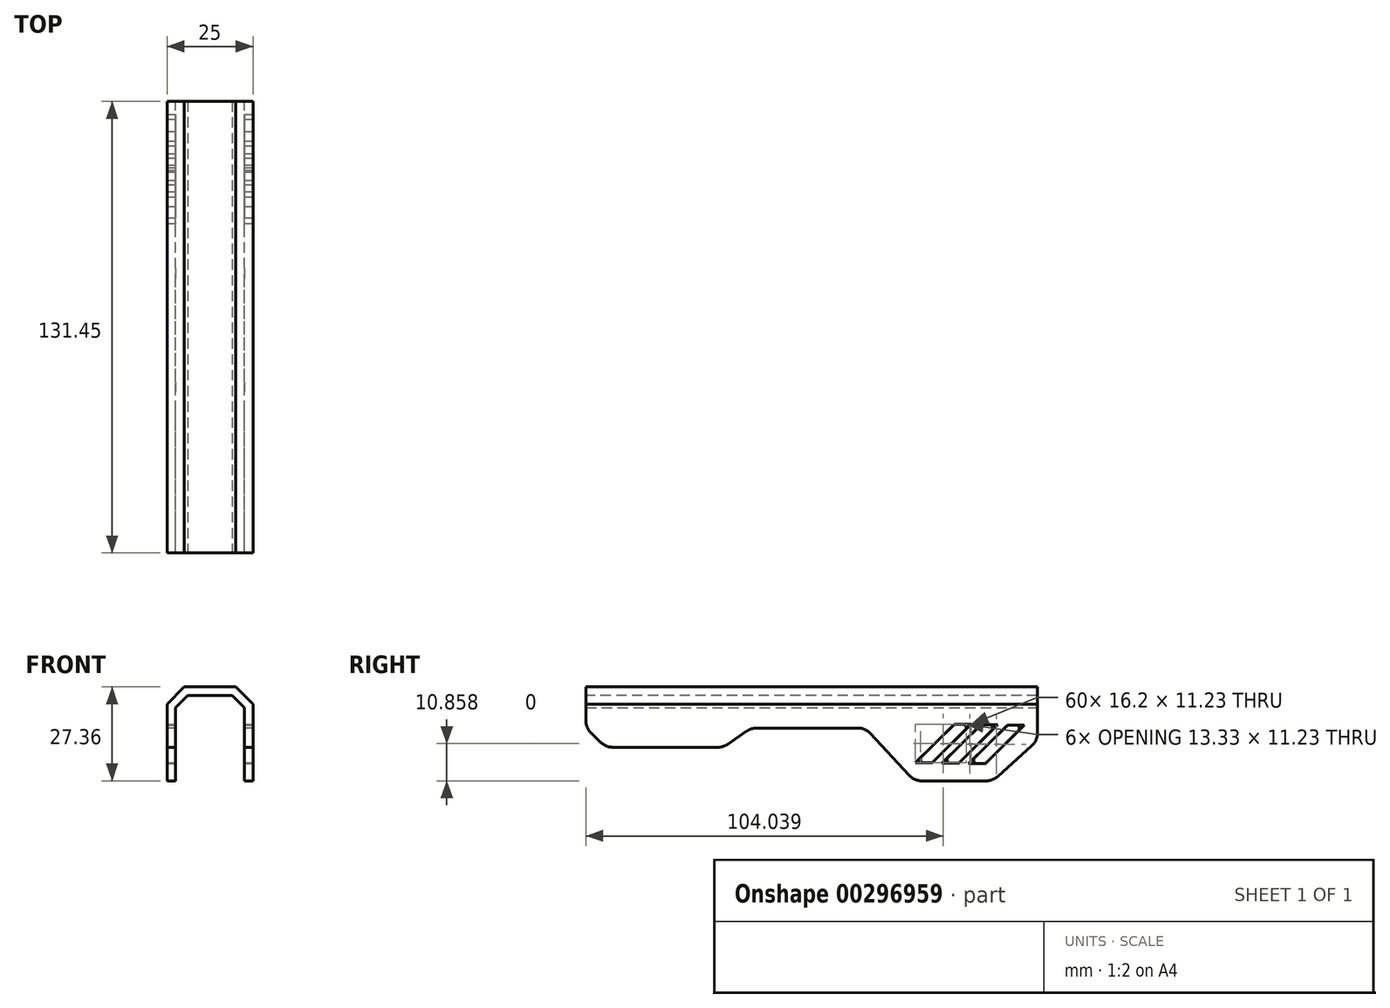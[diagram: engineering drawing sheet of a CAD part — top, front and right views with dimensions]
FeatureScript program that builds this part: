
annotation { "Feature Type Name" : "Feature", "Feature Type Description" : "" }
export const myFeature = defineFeature(function(context is Context, id is Id, definition is map)
    precondition{}
    {
        {
            var Q0;
            Q0=qCreatedBy(makeId("Right.planeOp"),FACE);
            var sketch = newSketch(context, id + "F0", { "sketchPlane" : qUnion([Q0])});
            skLineSegment(sketch, "E0.bottom", {"start": v(-66.9, 36.75) * mm, "end": v(64.56, 36.75) * mm});
            skLineSegment(sketch, "E0.top", {"start": v(-66.9, -14) * mm, "end": v(64.56, -14) * mm});
            skLineSegment(sketch, "E0.left", {"start": v(-66.9, 36.75) * mm, "end": v(-66.9, -14) * mm});
            skLineSegment(sketch, "E0.right", {"start": v(64.56, 36.75) * mm, "end": v(64.56, -14) * mm});
            skLineSegment(sketch, "E1", {"start": v(-66.9, 24.74) * mm, "end": v(-61.07, 19.17) * mm});
            skLineSegment(sketch, "E2", {"start": v(-61.07, 19.17) * mm, "end": v(-26.92, 19.17) * mm});
            skLineSegment(sketch, "E3", {"start": v(-26.92, 19.17) * mm, "end": v(-18.71, 24.77) * mm});
            skLineSegment(sketch, "E4", {"start": v(-18.71, 24.77) * mm, "end": v(14.48, 24.77) * mm});
            skLineSegment(sketch, "E5", {"start": v(14.48, 24.77) * mm, "end": v(28.75, 9.39) * mm});
            skLineSegment(sketch, "E6", {"start": v(28.75, 9.39) * mm, "end": v(51.52, 9.39) * mm});
            skLineSegment(sketch, "E7", {"start": v(51.52, 9.39) * mm, "end": v(64.56, 21.1) * mm});
            skSolve(sketch);
        }
        {
            var Q0;
            {var subQ2=sQuery(id+"F0.wireOp",EDGE,"E0.bottom");Q0=makeQuery(id+"F0.imprint","IMPRINT",FACE,{"disambiguationData":[TD([[makeQuery(id+"F0.imprint","IMPRINT",EDGE,{"derivedFrom":subQ2}),-1.0]])]});}
            extrude(context, id + "F1", {"entities" : qUnion([Q0]), "depth" : 25 * mm, "symmetric" : true});
        }
        {
            var Q0;
            Q0=makeQuery(id+"F1.opExtrude","CAP_EDGE",EDGE,{"disambiguationData":[OSD([sQuery(id+"F0.wireOp",EDGE,"E0.bottom")])],"isStart":false});
            var Q1;
            Q1=makeQuery(id+"F1.opExtrude","CAP_EDGE",EDGE,{"disambiguationData":[OSD([sQuery(id+"F0.wireOp",EDGE,"E0.bottom")])],"isStart":true});
            chamfer(context, id + "F2", {"entities" : qUnion([Q0, Q1]), "width" : 5 * mm, "tangentPropagation" : true});
        }
        {
            var Q0;
            Q0=makeQuery(id+"F1.opExtrude","SWEPT_FACE",FACE,{"disambiguationData":[OSD([sQuery(id+"F0.wireOp",EDGE,"E0.left")])]});
            var Q1;
            Q1=makeQuery(id+"F1.opExtrude","SWEPT_FACE",FACE,{"disambiguationData":[OSD([sQuery(id+"F0.wireOp",EDGE,"E1")])]});
            var Q2;
            Q2=makeQuery(id+"F1.opExtrude","SWEPT_FACE",FACE,{"disambiguationData":[OSD([sQuery(id+"F0.wireOp",EDGE,"E2")])]});
            var Q3;
            Q3=makeQuery(id+"F1.opExtrude","SWEPT_FACE",FACE,{"disambiguationData":[OSD([sQuery(id+"F0.wireOp",EDGE,"E3")])]});
            var Q4;
            Q4=makeQuery(id+"F1.opExtrude","SWEPT_FACE",FACE,{"disambiguationData":[OSD([sQuery(id+"F0.wireOp",EDGE,"E4")])]});
            var Q5;
            Q5=makeQuery(id+"F1.opExtrude","SWEPT_FACE",FACE,{"disambiguationData":[OSD([sQuery(id+"F0.wireOp",EDGE,"E5")])]});
            var Q6;
            Q6=makeQuery(id+"F1.opExtrude","SWEPT_FACE",FACE,{"disambiguationData":[OSD([sQuery(id+"F0.wireOp",EDGE,"E6")])]});
            var Q7;
            Q7=makeQuery(id+"F1.opExtrude","SWEPT_FACE",FACE,{"disambiguationData":[OSD([sQuery(id+"F0.wireOp",EDGE,"E7")])]});
            var Q8;
            Q8=makeQuery(id+"F1.opExtrude","SWEPT_FACE",FACE,{"disambiguationData":[OSD([sQuery(id+"F0.wireOp",EDGE,"E0.right")])]});
            shell(context, id + "F3", {"entities" : qUnion([Q0, Q1, Q2, Q3, Q4, Q5, Q6, Q7, Q8]), "thickness" : 2.5 * mm});
        }
        {
            var Q0;
            Q0=makeQuery(id+"F1.opExtrude","SWEPT_EDGE",EDGE,{"disambiguationData":[OSD([sQuery(id+"F0.wireOp",EDGE,"E0.left"),sQuery(id+"F0.wireOp",EDGE,"E1")])]});
            var Q1;
            Q1=makeQuery(id+"F1.opExtrude","SWEPT_EDGE",EDGE,{"disambiguationData":[OSD([sQuery(id+"F0.wireOp",EDGE,"E1"),sQuery(id+"F0.wireOp",EDGE,"E2")])]});
            var Q2;
            Q2=makeQuery(id+"F1.opExtrude","SWEPT_EDGE",EDGE,{"disambiguationData":[OSD([sQuery(id+"F0.wireOp",EDGE,"E2"),sQuery(id+"F0.wireOp",EDGE,"E3")])]});
            var Q3;
            Q3=makeQuery(id+"F1.opExtrude","SWEPT_EDGE",EDGE,{"disambiguationData":[OSD([sQuery(id+"F0.wireOp",EDGE,"E3"),sQuery(id+"F0.wireOp",EDGE,"E4")])]});
            var Q4;
            Q4=makeQuery(id+"F1.opExtrude","SWEPT_EDGE",EDGE,{"disambiguationData":[OSD([sQuery(id+"F0.wireOp",EDGE,"E4"),sQuery(id+"F0.wireOp",EDGE,"E5")])]});
            var Q5;
            Q5=makeQuery(id+"F1.opExtrude","SWEPT_EDGE",EDGE,{"disambiguationData":[OSD([sQuery(id+"F0.wireOp",EDGE,"E5"),sQuery(id+"F0.wireOp",EDGE,"E6")])]});
            var Q6;
            Q6=makeQuery(id+"F1.opExtrude","SWEPT_EDGE",EDGE,{"disambiguationData":[OSD([sQuery(id+"F0.wireOp",EDGE,"E6"),sQuery(id+"F0.wireOp",EDGE,"E7")])]});
            var Q7;
            Q7=makeQuery(id+"F1.opExtrude","SWEPT_EDGE",EDGE,{"disambiguationData":[OSD([sQuery(id+"F0.wireOp",EDGE,"E0.right"),sQuery(id+"F0.wireOp",EDGE,"E7")])]});
            var Q8;
            Q8=makeQuery(id+"F3.opShell","OFFSET_EDGE",EDGE,{"disambiguationData":[OSD([sQuery(id+"F0.wireOp",EDGE,"E0.left"),sQuery(id+"F0.wireOp",EDGE,"E1")])]});
            var Q9;
            Q9=makeQuery(id+"F3.opShell","OFFSET_EDGE",EDGE,{"disambiguationData":[OSD([sQuery(id+"F0.wireOp",EDGE,"E1"),sQuery(id+"F0.wireOp",EDGE,"E2")])]});
            var Q10;
            Q10=makeQuery(id+"F3.opShell","OFFSET_EDGE",EDGE,{"disambiguationData":[OSD([sQuery(id+"F0.wireOp",EDGE,"E2"),sQuery(id+"F0.wireOp",EDGE,"E3")])]});
            var Q11;
            Q11=makeQuery(id+"F3.opShell","OFFSET_EDGE",EDGE,{"disambiguationData":[OSD([sQuery(id+"F0.wireOp",EDGE,"E3"),sQuery(id+"F0.wireOp",EDGE,"E4")])]});
            var Q12;
            Q12=makeQuery(id+"F3.opShell","OFFSET_EDGE",EDGE,{"disambiguationData":[OSD([sQuery(id+"F0.wireOp",EDGE,"E4"),sQuery(id+"F0.wireOp",EDGE,"E5")])]});
            var Q13;
            Q13=makeQuery(id+"F3.opShell","OFFSET_EDGE",EDGE,{"disambiguationData":[OSD([sQuery(id+"F0.wireOp",EDGE,"E5"),sQuery(id+"F0.wireOp",EDGE,"E6")])]});
            var Q14;
            Q14=makeQuery(id+"F3.opShell","OFFSET_EDGE",EDGE,{"disambiguationData":[OSD([sQuery(id+"F0.wireOp",EDGE,"E6"),sQuery(id+"F0.wireOp",EDGE,"E7")])]});
            var Q15;
            Q15=makeQuery(id+"F3.opShell","OFFSET_EDGE",EDGE,{"disambiguationData":[OSD([sQuery(id+"F0.wireOp",EDGE,"E0.right"),sQuery(id+"F0.wireOp",EDGE,"E7")])]});
            fillet(context, id + "F4", {"entities" : qUnion([Q0, Q1, Q2, Q3, Q4, Q5, Q6, Q7, Q8, Q9, Q10, Q11, Q12, Q13, Q14, Q15]), "radius" : 5 * mm, "tangentPropagation" : true, "allowEdgeOverflow" : false});
        }
        {
            var Q0;
            Q0=qCreatedBy(makeId("Right.planeOp"),FACE);
            var sketch = newSketch(context, id + "F5", { "sketchPlane" : qUnion([Q0])});
            skLineSegment(sketch, "E8", {"start": v(60.73, 25.66) * mm, "end": v(49.4, 14.44) * mm});
            skLineSegment(sketch, "E9", {"start": v(49.4, 14.44) * mm, "end": v(44.53, 14.44) * mm});
            skLineSegment(sketch, "E10", {"start": v(44.53, 14.44) * mm, "end": v(55.87, 25.66) * mm});
            skLineSegment(sketch, "E11", {"start": v(55.87, 25.66) * mm, "end": v(60.73, 25.66) * mm});
            skLineSegment(sketch, "E12.1.0.0", {"start": v(36.8, 14.54) * mm, "end": v(48.13, 25.76) * mm});
            skLineSegment(sketch, "E12.1.0.1", {"start": v(52.99, 25.76) * mm, "end": v(41.65, 14.54) * mm});
            skLineSegment(sketch, "E12.1.0.2", {"start": v(48.13, 25.76) * mm, "end": v(52.99, 25.76) * mm});
            skLineSegment(sketch, "E12.1.0.3", {"start": v(41.65, 14.54) * mm, "end": v(36.8, 14.54) * mm});
            skLineSegment(sketch, "E12.2.0.0", {"start": v(29.05, 14.63) * mm, "end": v(40.39, 25.86) * mm});
            skLineSegment(sketch, "E12.2.0.1", {"start": v(45.25, 25.86) * mm, "end": v(33.91, 14.63) * mm});
            skLineSegment(sketch, "E12.2.0.2", {"start": v(40.39, 25.86) * mm, "end": v(45.25, 25.86) * mm});
            skLineSegment(sketch, "E12.2.0.3", {"start": v(33.91, 14.63) * mm, "end": v(29.05, 14.63) * mm});
            skLineSegment(sketch, "E12.direction1", {"start": v(44.53, 14.44) * mm, "end": v(36.8, 14.54) * mm, "construction": true});
            skSolve(sketch);
        }
        {
            var Q0;
            Q0 = qSketchRegion(id + "F5", true);
            extrude(context, id + "F6", {"entities" : qUnion([Q0]), "operationType" : NewBodyOperationType.REMOVE, "oppositeDirection" : true, "depth" : 25 * mm, "symmetric" : true});
        }
        {
            var Q0;
            {var subQ0=sQuery(id+"F0.wireOp",EDGE,"E7");var subQ1=sQuery(id+"F0.wireOp",EDGE,"E6");var subQ2=sQuery(id+"F0.wireOp",EDGE,"E5");var subQ3=sQuery(id+"F0.wireOp",EDGE,"E4");var subQ4=sQuery(id+"F0.wireOp",EDGE,"E3");var subQ5=sQuery(id+"F0.wireOp",EDGE,"E2");var subQ6=sQuery(id+"F0.wireOp",EDGE,"E1");var subQ7=sQuery(id+"F0.wireOp",EDGE,"E0.right");var subQ8=sQuery(id+"F0.wireOp",EDGE,"E0.left");var subQ9=sQuery(id+"F0.wireOp",EDGE,"E0.bottom");var subQ10=makeQuery(id+"F1.opExtrude","CAP_FACE",FACE,{"disambiguationData":[OSD([subQ9,subQ8,subQ7,subQ6,subQ5,subQ4,subQ3,subQ2,subQ1,subQ0])],"isStart":true});var subQ11=sQuery(id+"F5.wireOp",EDGE,"E8");var subQ12=sQuery(id+"F5.wireOp",EDGE,"E11");Q0=makeQuery(id+"F6.boolean.opBoolean","COPY",EDGE,{"disambiguationData":[TD([subQ10])],"derivedFrom":makeQuery(id+"F6.opExtrude","SWEPT_EDGE",EDGE,{"disambiguationData":[OSD([subQ11,subQ12])]})});}
            var Q1;
            {var subQ0=sQuery(id+"F0.wireOp",EDGE,"E7");var subQ1=sQuery(id+"F0.wireOp",EDGE,"E6");var subQ2=sQuery(id+"F0.wireOp",EDGE,"E5");var subQ3=sQuery(id+"F0.wireOp",EDGE,"E4");var subQ4=sQuery(id+"F0.wireOp",EDGE,"E3");var subQ5=sQuery(id+"F0.wireOp",EDGE,"E2");var subQ6=sQuery(id+"F0.wireOp",EDGE,"E1");var subQ7=sQuery(id+"F0.wireOp",EDGE,"E0.right");var subQ8=sQuery(id+"F0.wireOp",EDGE,"E0.left");var subQ9=sQuery(id+"F0.wireOp",EDGE,"E0.bottom");var subQ10=makeQuery(id+"F1.opExtrude","CAP_FACE",FACE,{"disambiguationData":[OSD([subQ9,subQ8,subQ7,subQ6,subQ5,subQ4,subQ3,subQ2,subQ1,subQ0])],"isStart":true});var subQ11=sQuery(id+"F5.wireOp",EDGE,"E11");var subQ12=sQuery(id+"F5.wireOp",EDGE,"E10");Q1=makeQuery(id+"F6.boolean.opBoolean","COPY",EDGE,{"disambiguationData":[TD([subQ10])],"derivedFrom":makeQuery(id+"F6.opExtrude","SWEPT_EDGE",EDGE,{"disambiguationData":[OSD([subQ12,subQ11])]})});}
            var Q2;
            {var subQ0=sQuery(id+"F0.wireOp",EDGE,"E7");var subQ1=sQuery(id+"F0.wireOp",EDGE,"E6");var subQ2=sQuery(id+"F0.wireOp",EDGE,"E5");var subQ3=sQuery(id+"F0.wireOp",EDGE,"E4");var subQ4=sQuery(id+"F0.wireOp",EDGE,"E3");var subQ5=sQuery(id+"F0.wireOp",EDGE,"E2");var subQ6=sQuery(id+"F0.wireOp",EDGE,"E1");var subQ7=sQuery(id+"F0.wireOp",EDGE,"E0.right");var subQ8=sQuery(id+"F0.wireOp",EDGE,"E0.left");var subQ9=sQuery(id+"F0.wireOp",EDGE,"E0.bottom");var subQ10=makeQuery(id+"F1.opExtrude","CAP_FACE",FACE,{"disambiguationData":[OSD([subQ9,subQ8,subQ7,subQ6,subQ5,subQ4,subQ3,subQ2,subQ1,subQ0])],"isStart":true});var subQ11=sQuery(id+"F5.wireOp",EDGE,"E9");var subQ12=sQuery(id+"F5.wireOp",EDGE,"E10");Q2=makeQuery(id+"F6.boolean.opBoolean","COPY",EDGE,{"disambiguationData":[TD([subQ10])],"derivedFrom":makeQuery(id+"F6.opExtrude","SWEPT_EDGE",EDGE,{"disambiguationData":[OSD([subQ11,subQ12])]})});}
            var Q3;
            {var subQ0=sQuery(id+"F0.wireOp",EDGE,"E7");var subQ1=sQuery(id+"F0.wireOp",EDGE,"E6");var subQ2=sQuery(id+"F0.wireOp",EDGE,"E5");var subQ3=sQuery(id+"F0.wireOp",EDGE,"E4");var subQ4=sQuery(id+"F0.wireOp",EDGE,"E3");var subQ5=sQuery(id+"F0.wireOp",EDGE,"E2");var subQ6=sQuery(id+"F0.wireOp",EDGE,"E1");var subQ7=sQuery(id+"F0.wireOp",EDGE,"E0.right");var subQ8=sQuery(id+"F0.wireOp",EDGE,"E0.left");var subQ9=sQuery(id+"F0.wireOp",EDGE,"E0.bottom");var subQ10=makeQuery(id+"F1.opExtrude","CAP_FACE",FACE,{"disambiguationData":[OSD([subQ9,subQ8,subQ7,subQ6,subQ5,subQ4,subQ3,subQ2,subQ1,subQ0])],"isStart":true});var subQ11=sQuery(id+"F5.wireOp",EDGE,"E12.1.0.0");var subQ12=sQuery(id+"F5.wireOp",EDGE,"E12.1.0.3");Q3=makeQuery(id+"F6.boolean.opBoolean","COPY",EDGE,{"disambiguationData":[TD([subQ10])],"derivedFrom":makeQuery(id+"F6.opExtrude","SWEPT_EDGE",EDGE,{"disambiguationData":[OSD([subQ11,subQ12])]})});}
            var Q4;
            {var subQ0=sQuery(id+"F0.wireOp",EDGE,"E7");var subQ1=sQuery(id+"F0.wireOp",EDGE,"E6");var subQ2=sQuery(id+"F0.wireOp",EDGE,"E5");var subQ3=sQuery(id+"F0.wireOp",EDGE,"E4");var subQ4=sQuery(id+"F0.wireOp",EDGE,"E3");var subQ5=sQuery(id+"F0.wireOp",EDGE,"E2");var subQ6=sQuery(id+"F0.wireOp",EDGE,"E1");var subQ7=sQuery(id+"F0.wireOp",EDGE,"E0.right");var subQ8=sQuery(id+"F0.wireOp",EDGE,"E0.left");var subQ9=sQuery(id+"F0.wireOp",EDGE,"E0.bottom");var subQ10=makeQuery(id+"F1.opExtrude","CAP_FACE",FACE,{"disambiguationData":[OSD([subQ9,subQ8,subQ7,subQ6,subQ5,subQ4,subQ3,subQ2,subQ1,subQ0])],"isStart":true});var subQ11=sQuery(id+"F5.wireOp",EDGE,"E12.2.0.0");var subQ12=sQuery(id+"F5.wireOp",EDGE,"E12.2.0.3");Q4=makeQuery(id+"F6.boolean.opBoolean","COPY",EDGE,{"disambiguationData":[TD([subQ10])],"derivedFrom":makeQuery(id+"F6.opExtrude","SWEPT_EDGE",EDGE,{"disambiguationData":[OSD([subQ11,subQ12])]})});}
            var Q5;
            {var subQ0=sQuery(id+"F0.wireOp",EDGE,"E7");var subQ1=sQuery(id+"F0.wireOp",EDGE,"E6");var subQ2=sQuery(id+"F0.wireOp",EDGE,"E5");var subQ3=sQuery(id+"F0.wireOp",EDGE,"E4");var subQ4=sQuery(id+"F0.wireOp",EDGE,"E3");var subQ5=sQuery(id+"F0.wireOp",EDGE,"E2");var subQ6=sQuery(id+"F0.wireOp",EDGE,"E1");var subQ7=sQuery(id+"F0.wireOp",EDGE,"E0.right");var subQ8=sQuery(id+"F0.wireOp",EDGE,"E0.left");var subQ9=sQuery(id+"F0.wireOp",EDGE,"E0.bottom");var subQ10=makeQuery(id+"F1.opExtrude","CAP_FACE",FACE,{"disambiguationData":[OSD([subQ9,subQ8,subQ7,subQ6,subQ5,subQ4,subQ3,subQ2,subQ1,subQ0])],"isStart":true});var subQ11=sQuery(id+"F5.wireOp",EDGE,"E8");var subQ12=sQuery(id+"F5.wireOp",EDGE,"E9");Q5=makeQuery(id+"F6.boolean.opBoolean","COPY",EDGE,{"disambiguationData":[TD([subQ10])],"derivedFrom":makeQuery(id+"F6.opExtrude","SWEPT_EDGE",EDGE,{"disambiguationData":[OSD([subQ11,subQ12])]})});}
            var Q6;
            {var subQ0=sQuery(id+"F0.wireOp",EDGE,"E7");var subQ1=sQuery(id+"F0.wireOp",EDGE,"E6");var subQ2=sQuery(id+"F0.wireOp",EDGE,"E5");var subQ3=sQuery(id+"F0.wireOp",EDGE,"E4");var subQ4=sQuery(id+"F0.wireOp",EDGE,"E3");var subQ5=sQuery(id+"F0.wireOp",EDGE,"E2");var subQ6=sQuery(id+"F0.wireOp",EDGE,"E1");var subQ7=sQuery(id+"F0.wireOp",EDGE,"E0.right");var subQ8=sQuery(id+"F0.wireOp",EDGE,"E0.left");var subQ9=sQuery(id+"F0.wireOp",EDGE,"E0.bottom");var subQ10=makeQuery(id+"F1.opExtrude","CAP_FACE",FACE,{"disambiguationData":[OSD([subQ9,subQ8,subQ7,subQ6,subQ5,subQ4,subQ3,subQ2,subQ1,subQ0])],"isStart":true});var subQ11=sQuery(id+"F5.wireOp",EDGE,"E12.1.0.3");var subQ12=sQuery(id+"F5.wireOp",EDGE,"E12.1.0.1");Q6=makeQuery(id+"F6.boolean.opBoolean","COPY",EDGE,{"disambiguationData":[TD([subQ10])],"derivedFrom":makeQuery(id+"F6.opExtrude","SWEPT_EDGE",EDGE,{"disambiguationData":[OSD([subQ12,subQ11])]})});}
            var Q7;
            {var subQ0=sQuery(id+"F0.wireOp",EDGE,"E7");var subQ1=sQuery(id+"F0.wireOp",EDGE,"E6");var subQ2=sQuery(id+"F0.wireOp",EDGE,"E5");var subQ3=sQuery(id+"F0.wireOp",EDGE,"E4");var subQ4=sQuery(id+"F0.wireOp",EDGE,"E3");var subQ5=sQuery(id+"F0.wireOp",EDGE,"E2");var subQ6=sQuery(id+"F0.wireOp",EDGE,"E1");var subQ7=sQuery(id+"F0.wireOp",EDGE,"E0.right");var subQ8=sQuery(id+"F0.wireOp",EDGE,"E0.left");var subQ9=sQuery(id+"F0.wireOp",EDGE,"E0.bottom");var subQ10=makeQuery(id+"F1.opExtrude","CAP_FACE",FACE,{"disambiguationData":[OSD([subQ9,subQ8,subQ7,subQ6,subQ5,subQ4,subQ3,subQ2,subQ1,subQ0])],"isStart":true});var subQ11=sQuery(id+"F5.wireOp",EDGE,"E12.2.0.1");var subQ12=sQuery(id+"F5.wireOp",EDGE,"E12.2.0.3");Q7=makeQuery(id+"F6.boolean.opBoolean","COPY",EDGE,{"disambiguationData":[TD([subQ10])],"derivedFrom":makeQuery(id+"F6.opExtrude","SWEPT_EDGE",EDGE,{"disambiguationData":[OSD([subQ11,subQ12])]})});}
            var Q8;
            {var subQ0=sQuery(id+"F0.wireOp",EDGE,"E7");var subQ1=sQuery(id+"F0.wireOp",EDGE,"E6");var subQ2=sQuery(id+"F0.wireOp",EDGE,"E5");var subQ3=sQuery(id+"F0.wireOp",EDGE,"E4");var subQ4=sQuery(id+"F0.wireOp",EDGE,"E3");var subQ5=sQuery(id+"F0.wireOp",EDGE,"E2");var subQ6=sQuery(id+"F0.wireOp",EDGE,"E1");var subQ7=sQuery(id+"F0.wireOp",EDGE,"E0.right");var subQ8=sQuery(id+"F0.wireOp",EDGE,"E0.left");var subQ9=sQuery(id+"F0.wireOp",EDGE,"E0.bottom");var subQ10=makeQuery(id+"F1.opExtrude","CAP_FACE",FACE,{"disambiguationData":[OSD([subQ9,subQ8,subQ7,subQ6,subQ5,subQ4,subQ3,subQ2,subQ1,subQ0])],"isStart":true});var subQ11=sQuery(id+"F5.wireOp",EDGE,"E12.1.0.2");var subQ12=sQuery(id+"F5.wireOp",EDGE,"E12.1.0.1");Q8=makeQuery(id+"F6.boolean.opBoolean","COPY",EDGE,{"disambiguationData":[TD([subQ10])],"derivedFrom":makeQuery(id+"F6.opExtrude","SWEPT_EDGE",EDGE,{"disambiguationData":[OSD([subQ12,subQ11])]})});}
            var Q9;
            {var subQ0=sQuery(id+"F0.wireOp",EDGE,"E7");var subQ1=sQuery(id+"F0.wireOp",EDGE,"E6");var subQ2=sQuery(id+"F0.wireOp",EDGE,"E5");var subQ3=sQuery(id+"F0.wireOp",EDGE,"E4");var subQ4=sQuery(id+"F0.wireOp",EDGE,"E3");var subQ5=sQuery(id+"F0.wireOp",EDGE,"E2");var subQ6=sQuery(id+"F0.wireOp",EDGE,"E1");var subQ7=sQuery(id+"F0.wireOp",EDGE,"E0.right");var subQ8=sQuery(id+"F0.wireOp",EDGE,"E0.left");var subQ9=sQuery(id+"F0.wireOp",EDGE,"E0.bottom");var subQ10=makeQuery(id+"F1.opExtrude","CAP_FACE",FACE,{"disambiguationData":[OSD([subQ9,subQ8,subQ7,subQ6,subQ5,subQ4,subQ3,subQ2,subQ1,subQ0])],"isStart":true});var subQ11=sQuery(id+"F5.wireOp",EDGE,"E12.2.0.1");var subQ12=sQuery(id+"F5.wireOp",EDGE,"E12.2.0.2");Q9=makeQuery(id+"F6.boolean.opBoolean","COPY",EDGE,{"disambiguationData":[TD([subQ10])],"derivedFrom":makeQuery(id+"F6.opExtrude","SWEPT_EDGE",EDGE,{"disambiguationData":[OSD([subQ11,subQ12])]})});}
            var Q10;
            {var subQ0=sQuery(id+"F0.wireOp",EDGE,"E7");var subQ1=sQuery(id+"F0.wireOp",EDGE,"E6");var subQ2=sQuery(id+"F0.wireOp",EDGE,"E5");var subQ3=sQuery(id+"F0.wireOp",EDGE,"E4");var subQ4=sQuery(id+"F0.wireOp",EDGE,"E3");var subQ5=sQuery(id+"F0.wireOp",EDGE,"E2");var subQ6=sQuery(id+"F0.wireOp",EDGE,"E1");var subQ7=sQuery(id+"F0.wireOp",EDGE,"E0.right");var subQ8=sQuery(id+"F0.wireOp",EDGE,"E0.left");var subQ9=sQuery(id+"F0.wireOp",EDGE,"E0.bottom");var subQ10=makeQuery(id+"F1.opExtrude","CAP_FACE",FACE,{"disambiguationData":[OSD([subQ9,subQ8,subQ7,subQ6,subQ5,subQ4,subQ3,subQ2,subQ1,subQ0])],"isStart":true});var subQ11=sQuery(id+"F5.wireOp",EDGE,"E12.2.0.2");var subQ12=sQuery(id+"F5.wireOp",EDGE,"E12.2.0.0");Q10=makeQuery(id+"F6.boolean.opBoolean","COPY",EDGE,{"disambiguationData":[TD([subQ10])],"derivedFrom":makeQuery(id+"F6.opExtrude","SWEPT_EDGE",EDGE,{"disambiguationData":[OSD([subQ12,subQ11])]})});}
            var Q11;
            {var subQ0=sQuery(id+"F0.wireOp",EDGE,"E7");var subQ1=sQuery(id+"F0.wireOp",EDGE,"E6");var subQ2=sQuery(id+"F0.wireOp",EDGE,"E5");var subQ3=sQuery(id+"F0.wireOp",EDGE,"E4");var subQ4=sQuery(id+"F0.wireOp",EDGE,"E3");var subQ5=sQuery(id+"F0.wireOp",EDGE,"E2");var subQ6=sQuery(id+"F0.wireOp",EDGE,"E1");var subQ7=sQuery(id+"F0.wireOp",EDGE,"E0.right");var subQ8=sQuery(id+"F0.wireOp",EDGE,"E0.left");var subQ9=sQuery(id+"F0.wireOp",EDGE,"E0.bottom");var subQ10=makeQuery(id+"F1.opExtrude","CAP_FACE",FACE,{"disambiguationData":[OSD([subQ9,subQ8,subQ7,subQ6,subQ5,subQ4,subQ3,subQ2,subQ1,subQ0])],"isStart":true});var subQ11=sQuery(id+"F5.wireOp",EDGE,"E12.1.0.2");var subQ12=sQuery(id+"F5.wireOp",EDGE,"E12.1.0.0");Q11=makeQuery(id+"F6.boolean.opBoolean","COPY",EDGE,{"disambiguationData":[TD([subQ10])],"derivedFrom":makeQuery(id+"F6.opExtrude","SWEPT_EDGE",EDGE,{"disambiguationData":[OSD([subQ12,subQ11])]})});}
            var Q12;
            {var subQ0=sQuery(id+"F0.wireOp",EDGE,"E7");var subQ1=sQuery(id+"F0.wireOp",EDGE,"E6");var subQ2=sQuery(id+"F0.wireOp",EDGE,"E5");var subQ3=sQuery(id+"F0.wireOp",EDGE,"E4");var subQ4=sQuery(id+"F0.wireOp",EDGE,"E3");var subQ5=sQuery(id+"F0.wireOp",EDGE,"E2");var subQ6=sQuery(id+"F0.wireOp",EDGE,"E1");var subQ7=sQuery(id+"F0.wireOp",EDGE,"E0.right");var subQ8=sQuery(id+"F0.wireOp",EDGE,"E0.left");var subQ9=sQuery(id+"F0.wireOp",EDGE,"E0.bottom");var subQ10=makeQuery(id+"F1.opExtrude","CAP_FACE",FACE,{"disambiguationData":[OSD([subQ9,subQ8,subQ7,subQ6,subQ5,subQ4,subQ3,subQ2,subQ1,subQ0])],"isStart":false});var subQ11=sQuery(id+"F5.wireOp",EDGE,"E8");var subQ12=sQuery(id+"F5.wireOp",EDGE,"E11");Q12=makeQuery(id+"F6.boolean.opBoolean","COPY",EDGE,{"disambiguationData":[TD([subQ10])],"derivedFrom":makeQuery(id+"F6.opExtrude","SWEPT_EDGE",EDGE,{"disambiguationData":[OSD([subQ11,subQ12])]})});}
            var Q13;
            {var subQ0=sQuery(id+"F0.wireOp",EDGE,"E7");var subQ1=sQuery(id+"F0.wireOp",EDGE,"E6");var subQ2=sQuery(id+"F0.wireOp",EDGE,"E5");var subQ3=sQuery(id+"F0.wireOp",EDGE,"E4");var subQ4=sQuery(id+"F0.wireOp",EDGE,"E3");var subQ5=sQuery(id+"F0.wireOp",EDGE,"E2");var subQ6=sQuery(id+"F0.wireOp",EDGE,"E1");var subQ7=sQuery(id+"F0.wireOp",EDGE,"E0.right");var subQ8=sQuery(id+"F0.wireOp",EDGE,"E0.left");var subQ9=sQuery(id+"F0.wireOp",EDGE,"E0.bottom");var subQ10=makeQuery(id+"F1.opExtrude","CAP_FACE",FACE,{"disambiguationData":[OSD([subQ9,subQ8,subQ7,subQ6,subQ5,subQ4,subQ3,subQ2,subQ1,subQ0])],"isStart":false});var subQ11=sQuery(id+"F5.wireOp",EDGE,"E12.1.0.1");var subQ12=sQuery(id+"F5.wireOp",EDGE,"E12.1.0.2");Q13=makeQuery(id+"F6.boolean.opBoolean","COPY",EDGE,{"disambiguationData":[TD([subQ10])],"derivedFrom":makeQuery(id+"F6.opExtrude","SWEPT_EDGE",EDGE,{"disambiguationData":[OSD([subQ11,subQ12])]})});}
            var Q14;
            {var subQ0=sQuery(id+"F0.wireOp",EDGE,"E7");var subQ1=sQuery(id+"F0.wireOp",EDGE,"E6");var subQ2=sQuery(id+"F0.wireOp",EDGE,"E5");var subQ3=sQuery(id+"F0.wireOp",EDGE,"E4");var subQ4=sQuery(id+"F0.wireOp",EDGE,"E3");var subQ5=sQuery(id+"F0.wireOp",EDGE,"E2");var subQ6=sQuery(id+"F0.wireOp",EDGE,"E1");var subQ7=sQuery(id+"F0.wireOp",EDGE,"E0.right");var subQ8=sQuery(id+"F0.wireOp",EDGE,"E0.left");var subQ9=sQuery(id+"F0.wireOp",EDGE,"E0.bottom");var subQ10=makeQuery(id+"F1.opExtrude","CAP_FACE",FACE,{"disambiguationData":[OSD([subQ9,subQ8,subQ7,subQ6,subQ5,subQ4,subQ3,subQ2,subQ1,subQ0])],"isStart":false});var subQ11=sQuery(id+"F5.wireOp",EDGE,"E12.2.0.2");var subQ12=sQuery(id+"F5.wireOp",EDGE,"E12.2.0.1");Q14=makeQuery(id+"F6.boolean.opBoolean","COPY",EDGE,{"disambiguationData":[TD([subQ10])],"derivedFrom":makeQuery(id+"F6.opExtrude","SWEPT_EDGE",EDGE,{"disambiguationData":[OSD([subQ12,subQ11])]})});}
            var Q15;
            {var subQ0=sQuery(id+"F0.wireOp",EDGE,"E7");var subQ1=sQuery(id+"F0.wireOp",EDGE,"E6");var subQ2=sQuery(id+"F0.wireOp",EDGE,"E5");var subQ3=sQuery(id+"F0.wireOp",EDGE,"E4");var subQ4=sQuery(id+"F0.wireOp",EDGE,"E3");var subQ5=sQuery(id+"F0.wireOp",EDGE,"E2");var subQ6=sQuery(id+"F0.wireOp",EDGE,"E1");var subQ7=sQuery(id+"F0.wireOp",EDGE,"E0.right");var subQ8=sQuery(id+"F0.wireOp",EDGE,"E0.left");var subQ9=sQuery(id+"F0.wireOp",EDGE,"E0.bottom");var subQ10=makeQuery(id+"F1.opExtrude","CAP_FACE",FACE,{"disambiguationData":[OSD([subQ9,subQ8,subQ7,subQ6,subQ5,subQ4,subQ3,subQ2,subQ1,subQ0])],"isStart":false});var subQ11=sQuery(id+"F5.wireOp",EDGE,"E8");var subQ12=sQuery(id+"F5.wireOp",EDGE,"E9");Q15=makeQuery(id+"F6.boolean.opBoolean","COPY",EDGE,{"disambiguationData":[TD([subQ10])],"derivedFrom":makeQuery(id+"F6.opExtrude","SWEPT_EDGE",EDGE,{"disambiguationData":[OSD([subQ11,subQ12])]})});}
            var Q16;
            {var subQ0=sQuery(id+"F0.wireOp",EDGE,"E7");var subQ1=sQuery(id+"F0.wireOp",EDGE,"E6");var subQ2=sQuery(id+"F0.wireOp",EDGE,"E5");var subQ3=sQuery(id+"F0.wireOp",EDGE,"E4");var subQ4=sQuery(id+"F0.wireOp",EDGE,"E3");var subQ5=sQuery(id+"F0.wireOp",EDGE,"E2");var subQ6=sQuery(id+"F0.wireOp",EDGE,"E1");var subQ7=sQuery(id+"F0.wireOp",EDGE,"E0.right");var subQ8=sQuery(id+"F0.wireOp",EDGE,"E0.left");var subQ9=sQuery(id+"F0.wireOp",EDGE,"E0.bottom");var subQ10=makeQuery(id+"F1.opExtrude","CAP_FACE",FACE,{"disambiguationData":[OSD([subQ9,subQ8,subQ7,subQ6,subQ5,subQ4,subQ3,subQ2,subQ1,subQ0])],"isStart":false});var subQ11=sQuery(id+"F5.wireOp",EDGE,"E12.1.0.3");var subQ12=sQuery(id+"F5.wireOp",EDGE,"E12.1.0.1");Q16=makeQuery(id+"F6.boolean.opBoolean","COPY",EDGE,{"disambiguationData":[TD([subQ10])],"derivedFrom":makeQuery(id+"F6.opExtrude","SWEPT_EDGE",EDGE,{"disambiguationData":[OSD([subQ12,subQ11])]})});}
            var Q17;
            {var subQ0=sQuery(id+"F0.wireOp",EDGE,"E7");var subQ1=sQuery(id+"F0.wireOp",EDGE,"E6");var subQ2=sQuery(id+"F0.wireOp",EDGE,"E5");var subQ3=sQuery(id+"F0.wireOp",EDGE,"E4");var subQ4=sQuery(id+"F0.wireOp",EDGE,"E3");var subQ5=sQuery(id+"F0.wireOp",EDGE,"E2");var subQ6=sQuery(id+"F0.wireOp",EDGE,"E1");var subQ7=sQuery(id+"F0.wireOp",EDGE,"E0.right");var subQ8=sQuery(id+"F0.wireOp",EDGE,"E0.left");var subQ9=sQuery(id+"F0.wireOp",EDGE,"E0.bottom");var subQ10=makeQuery(id+"F1.opExtrude","CAP_FACE",FACE,{"disambiguationData":[OSD([subQ9,subQ8,subQ7,subQ6,subQ5,subQ4,subQ3,subQ2,subQ1,subQ0])],"isStart":false});var subQ11=sQuery(id+"F5.wireOp",EDGE,"E12.2.0.3");var subQ12=sQuery(id+"F5.wireOp",EDGE,"E12.2.0.1");Q17=makeQuery(id+"F6.boolean.opBoolean","COPY",EDGE,{"disambiguationData":[TD([subQ10])],"derivedFrom":makeQuery(id+"F6.opExtrude","SWEPT_EDGE",EDGE,{"disambiguationData":[OSD([subQ12,subQ11])]})});}
            var Q18;
            {var subQ0=sQuery(id+"F0.wireOp",EDGE,"E7");var subQ1=sQuery(id+"F0.wireOp",EDGE,"E6");var subQ2=sQuery(id+"F0.wireOp",EDGE,"E5");var subQ3=sQuery(id+"F0.wireOp",EDGE,"E4");var subQ4=sQuery(id+"F0.wireOp",EDGE,"E3");var subQ5=sQuery(id+"F0.wireOp",EDGE,"E2");var subQ6=sQuery(id+"F0.wireOp",EDGE,"E1");var subQ7=sQuery(id+"F0.wireOp",EDGE,"E0.right");var subQ8=sQuery(id+"F0.wireOp",EDGE,"E0.left");var subQ9=sQuery(id+"F0.wireOp",EDGE,"E0.bottom");var subQ10=makeQuery(id+"F1.opExtrude","CAP_FACE",FACE,{"disambiguationData":[OSD([subQ9,subQ8,subQ7,subQ6,subQ5,subQ4,subQ3,subQ2,subQ1,subQ0])],"isStart":false});var subQ11=sQuery(id+"F5.wireOp",EDGE,"E12.2.0.2");var subQ12=sQuery(id+"F5.wireOp",EDGE,"E12.2.0.0");Q18=makeQuery(id+"F6.boolean.opBoolean","COPY",EDGE,{"disambiguationData":[TD([subQ10])],"derivedFrom":makeQuery(id+"F6.opExtrude","SWEPT_EDGE",EDGE,{"disambiguationData":[OSD([subQ12,subQ11])]})});}
            var Q19;
            {var subQ0=sQuery(id+"F0.wireOp",EDGE,"E7");var subQ1=sQuery(id+"F0.wireOp",EDGE,"E6");var subQ2=sQuery(id+"F0.wireOp",EDGE,"E5");var subQ3=sQuery(id+"F0.wireOp",EDGE,"E4");var subQ4=sQuery(id+"F0.wireOp",EDGE,"E3");var subQ5=sQuery(id+"F0.wireOp",EDGE,"E2");var subQ6=sQuery(id+"F0.wireOp",EDGE,"E1");var subQ7=sQuery(id+"F0.wireOp",EDGE,"E0.right");var subQ8=sQuery(id+"F0.wireOp",EDGE,"E0.left");var subQ9=sQuery(id+"F0.wireOp",EDGE,"E0.bottom");var subQ10=makeQuery(id+"F1.opExtrude","CAP_FACE",FACE,{"disambiguationData":[OSD([subQ9,subQ8,subQ7,subQ6,subQ5,subQ4,subQ3,subQ2,subQ1,subQ0])],"isStart":false});var subQ11=sQuery(id+"F5.wireOp",EDGE,"E12.1.0.0");var subQ12=sQuery(id+"F5.wireOp",EDGE,"E12.1.0.2");Q19=makeQuery(id+"F6.boolean.opBoolean","COPY",EDGE,{"disambiguationData":[TD([subQ10])],"derivedFrom":makeQuery(id+"F6.opExtrude","SWEPT_EDGE",EDGE,{"disambiguationData":[OSD([subQ11,subQ12])]})});}
            var Q20;
            {var subQ0=sQuery(id+"F0.wireOp",EDGE,"E7");var subQ1=sQuery(id+"F0.wireOp",EDGE,"E6");var subQ2=sQuery(id+"F0.wireOp",EDGE,"E5");var subQ3=sQuery(id+"F0.wireOp",EDGE,"E4");var subQ4=sQuery(id+"F0.wireOp",EDGE,"E3");var subQ5=sQuery(id+"F0.wireOp",EDGE,"E2");var subQ6=sQuery(id+"F0.wireOp",EDGE,"E1");var subQ7=sQuery(id+"F0.wireOp",EDGE,"E0.right");var subQ8=sQuery(id+"F0.wireOp",EDGE,"E0.left");var subQ9=sQuery(id+"F0.wireOp",EDGE,"E0.bottom");var subQ10=makeQuery(id+"F1.opExtrude","CAP_FACE",FACE,{"disambiguationData":[OSD([subQ9,subQ8,subQ7,subQ6,subQ5,subQ4,subQ3,subQ2,subQ1,subQ0])],"isStart":false});var subQ11=sQuery(id+"F5.wireOp",EDGE,"E10");var subQ12=sQuery(id+"F5.wireOp",EDGE,"E11");Q20=makeQuery(id+"F6.boolean.opBoolean","COPY",EDGE,{"disambiguationData":[TD([subQ10])],"derivedFrom":makeQuery(id+"F6.opExtrude","SWEPT_EDGE",EDGE,{"disambiguationData":[OSD([subQ11,subQ12])]})});}
            var Q21;
            {var subQ0=sQuery(id+"F0.wireOp",EDGE,"E7");var subQ1=sQuery(id+"F0.wireOp",EDGE,"E6");var subQ2=sQuery(id+"F0.wireOp",EDGE,"E5");var subQ3=sQuery(id+"F0.wireOp",EDGE,"E4");var subQ4=sQuery(id+"F0.wireOp",EDGE,"E3");var subQ5=sQuery(id+"F0.wireOp",EDGE,"E2");var subQ6=sQuery(id+"F0.wireOp",EDGE,"E1");var subQ7=sQuery(id+"F0.wireOp",EDGE,"E0.right");var subQ8=sQuery(id+"F0.wireOp",EDGE,"E0.left");var subQ9=sQuery(id+"F0.wireOp",EDGE,"E0.bottom");var subQ10=makeQuery(id+"F1.opExtrude","CAP_FACE",FACE,{"disambiguationData":[OSD([subQ9,subQ8,subQ7,subQ6,subQ5,subQ4,subQ3,subQ2,subQ1,subQ0])],"isStart":false});var subQ11=sQuery(id+"F5.wireOp",EDGE,"E12.2.0.0");var subQ12=sQuery(id+"F5.wireOp",EDGE,"E12.2.0.3");Q21=makeQuery(id+"F6.boolean.opBoolean","COPY",EDGE,{"disambiguationData":[TD([subQ10])],"derivedFrom":makeQuery(id+"F6.opExtrude","SWEPT_EDGE",EDGE,{"disambiguationData":[OSD([subQ11,subQ12])]})});}
            var Q22;
            {var subQ0=sQuery(id+"F0.wireOp",EDGE,"E7");var subQ1=sQuery(id+"F0.wireOp",EDGE,"E6");var subQ2=sQuery(id+"F0.wireOp",EDGE,"E5");var subQ3=sQuery(id+"F0.wireOp",EDGE,"E4");var subQ4=sQuery(id+"F0.wireOp",EDGE,"E3");var subQ5=sQuery(id+"F0.wireOp",EDGE,"E2");var subQ6=sQuery(id+"F0.wireOp",EDGE,"E1");var subQ7=sQuery(id+"F0.wireOp",EDGE,"E0.right");var subQ8=sQuery(id+"F0.wireOp",EDGE,"E0.left");var subQ9=sQuery(id+"F0.wireOp",EDGE,"E0.bottom");var subQ10=makeQuery(id+"F1.opExtrude","CAP_FACE",FACE,{"disambiguationData":[OSD([subQ9,subQ8,subQ7,subQ6,subQ5,subQ4,subQ3,subQ2,subQ1,subQ0])],"isStart":false});var subQ11=sQuery(id+"F5.wireOp",EDGE,"E12.1.0.0");var subQ12=sQuery(id+"F5.wireOp",EDGE,"E12.1.0.3");Q22=makeQuery(id+"F6.boolean.opBoolean","COPY",EDGE,{"disambiguationData":[TD([subQ10])],"derivedFrom":makeQuery(id+"F6.opExtrude","SWEPT_EDGE",EDGE,{"disambiguationData":[OSD([subQ11,subQ12])]})});}
            var Q23;
            {var subQ0=sQuery(id+"F0.wireOp",EDGE,"E7");var subQ1=sQuery(id+"F0.wireOp",EDGE,"E6");var subQ2=sQuery(id+"F0.wireOp",EDGE,"E5");var subQ3=sQuery(id+"F0.wireOp",EDGE,"E4");var subQ4=sQuery(id+"F0.wireOp",EDGE,"E3");var subQ5=sQuery(id+"F0.wireOp",EDGE,"E2");var subQ6=sQuery(id+"F0.wireOp",EDGE,"E1");var subQ7=sQuery(id+"F0.wireOp",EDGE,"E0.right");var subQ8=sQuery(id+"F0.wireOp",EDGE,"E0.left");var subQ9=sQuery(id+"F0.wireOp",EDGE,"E0.bottom");var subQ10=makeQuery(id+"F1.opExtrude","CAP_FACE",FACE,{"disambiguationData":[OSD([subQ9,subQ8,subQ7,subQ6,subQ5,subQ4,subQ3,subQ2,subQ1,subQ0])],"isStart":false});var subQ11=sQuery(id+"F5.wireOp",EDGE,"E9");var subQ12=sQuery(id+"F5.wireOp",EDGE,"E10");Q23=makeQuery(id+"F6.boolean.opBoolean","COPY",EDGE,{"disambiguationData":[TD([subQ10])],"derivedFrom":makeQuery(id+"F6.opExtrude","SWEPT_EDGE",EDGE,{"disambiguationData":[OSD([subQ11,subQ12])]})});}
            fillet(context, id + "F7", {"entities" : qUnion([Q0, Q1, Q2, Q3, Q4, Q5, Q6, Q7, Q8, Q9, Q10, Q11, Q12, Q13, Q14, Q15, Q16, Q17, Q18, Q19, Q20, Q21, Q22, Q23]), "radius" : 1 * mm, "tangentPropagation" : true, "allowEdgeOverflow" : false});
        }
    });
